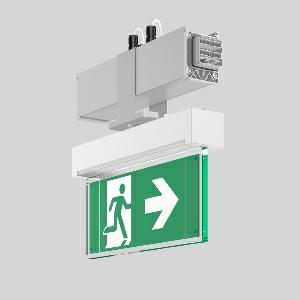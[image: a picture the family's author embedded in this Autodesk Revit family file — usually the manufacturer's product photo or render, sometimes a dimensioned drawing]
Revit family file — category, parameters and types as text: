
# Revit family: linedo_module_rz_9503rz_760_430_023_bd96
name_source: partatom
category: Lighting Fixtures
units: mm (PartAtom-declared; Revit-internal decimal feet)

## family parameters
Cut with Voids When Loaded = No
Host = Face
Light Source = No
Part Type = Normal
Room Calculation Point = No
Round Connector Dimension = Use Diameter
Shared = No

## types (1)
- LINEDO Module RZ
    Apparent Load = 0 VA
    Default Elevation = 1800 mm
    Description = LINEDO, silver, on/off
Continuous line luminaire, L 336 B 62 H 308, SBS, 3 h, automatischer Selbsttest
    Height = 308 mm
    Lamp = 0 x
    Length = 336 mm
    Luminous efficacy = 0 lm/W
    Manufacturer = RZB
    ModVariant = No
    Model = 9503RZ.760.430.023
    Mounting Place = Ceiling
    Mounting Type = Surface mounted
    Number of Poles = 1
    OnlyDefault = Yes
    Power Factor = 1
    Product Name = LINEDO Module RZ
    Product group = Continuous line luminaire system Linedo IP 54
    ProductGroupID = 314
    Protection Class = Protection class I
    Protection Degree = IP 54
    RLX_Detail_Level = 1
    RLX_Emergency_Light_Flux = 0 lm
    RLX_Emergency_Type = 0
    RLX_Emergency_Type_DB = No
    RlxData = <blob elided: 34821 chars, md5=4448357d>
    Standby Power = 0 W
    System Light Flux = 0 lm
    System Power = 0 W
    Type Comments = Product without accessories
    Type Image = 9503rz.760.434.023.jpg
    URL = http://relux.com
    VarID = ---
    Voltage = 0 V
    Weight = 0.00 kg
    Width = 62 mm

## geometry (parser evidence)
native form markers: Blend x4, Sweep x10
no freeform markers — native parametric forms only
